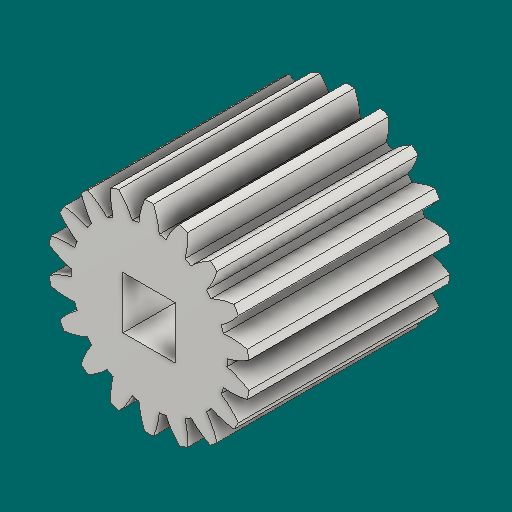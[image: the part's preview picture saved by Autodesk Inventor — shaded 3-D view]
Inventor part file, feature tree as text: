
AUTODESK INVENTOR PART (.ipt)
format: ipt  version: 2023.1 (Build 271208000, 208)  size: 340,992 bytes
history: native  units: in
note: dims shown in document units (in); Inventor stores cm internally (conversion verified against a paired STEP export)
features: other x12, sketch x5, plane x3
ambient origin geometry x8: Origin, YZ Plane, XZ Plane, XY Plane, X Axis, Y Axis, Z Axis, Center Point
bodies: Solid1 (feature_tree)
feature tree (20):
  other  "Spur Gear1"
  other  "Solid1::Spur Gear1"
  other  "TaggingFeature1"
  sketch  "Sketch1"  dims[d0=0.3937in]
  sketch  "Sketch2"  dims[d9=0.0in]
  sketch  "Sketch3"  dims[d14=0.0in]
  sketch  "Sketch4"  dims[d15=0.9in]
  sketch  "Sketch5"  dims[d16=0.0in d17=0.0in d18=0.0in d19=0.9in]
  plane  "XZ Plane_1"
  plane  "Work Plane2"
  plane  "Work Plane3"
  other  "Srf1"
  other  "Srf1::Derived"
  other  "Start plane iMate"
  other  "Distance iMate"
  other  "Position iMate"
  other  "Mesh iMate"
  other  "Axis iMate"
  other  "Mesh iMate2"
  other  "Align iMate"
